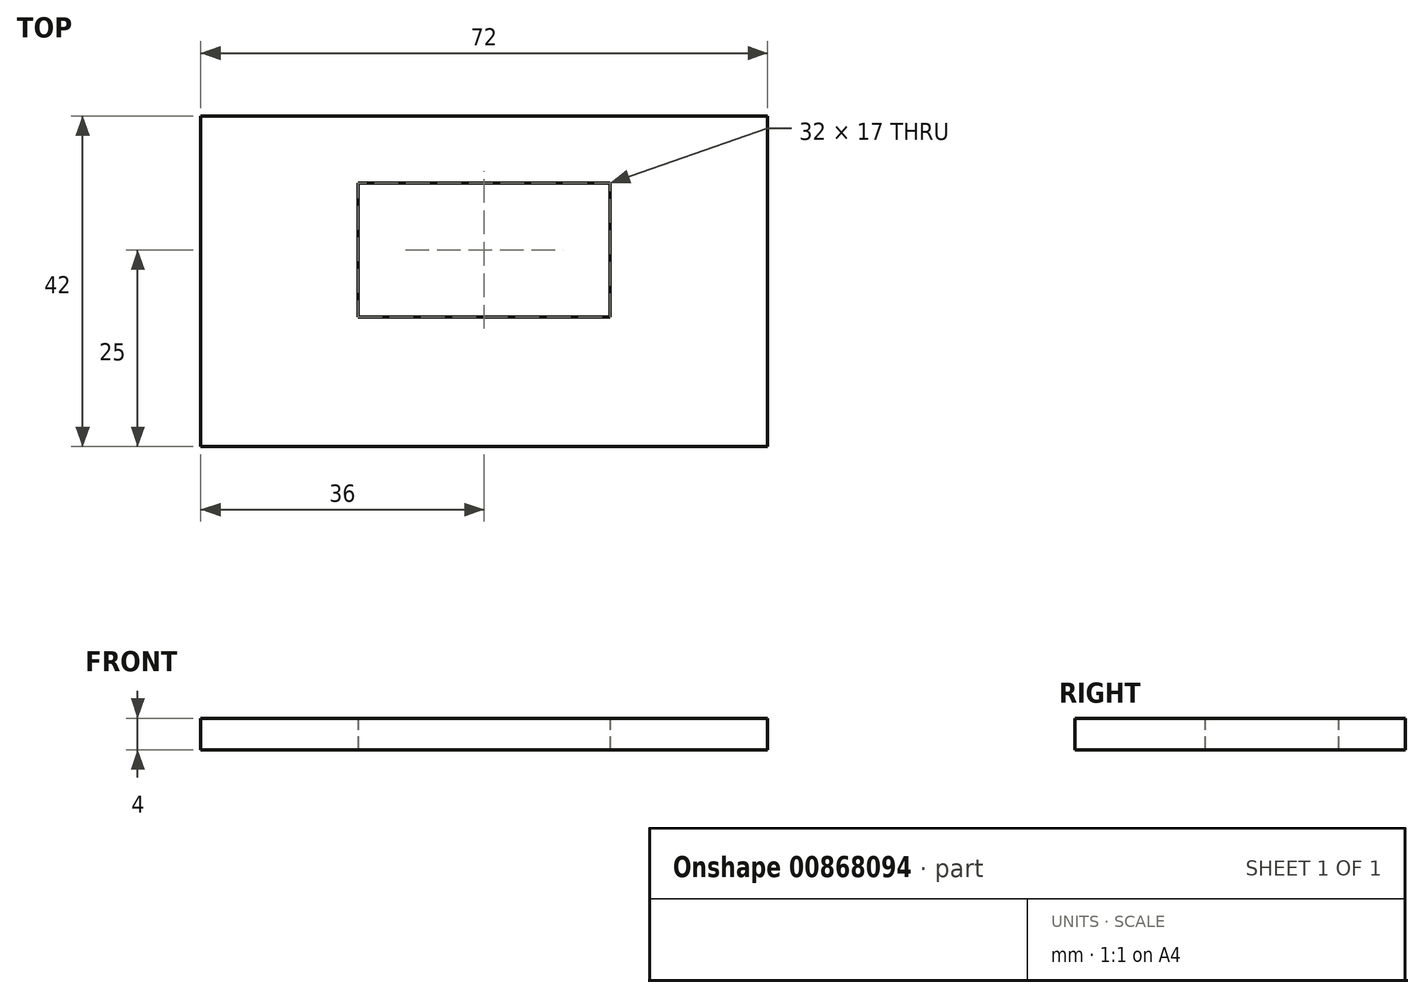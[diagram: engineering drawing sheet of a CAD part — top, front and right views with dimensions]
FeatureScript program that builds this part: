
annotation { "Feature Type Name" : "Feature", "Feature Type Description" : "" }
export const myFeature = defineFeature(function(context is Context, id is Id, definition is map)
    precondition{}
    {
        {
            var Q0;
            Q0=qCreatedBy(makeId("Top.planeOp"),FACE);
            var sketch = newSketch(context, id + "F0", { "sketchPlane" : qUnion([Q0])});
            skLineSegment(sketch, "E0.bottom", {"start": v(36, -21) * mm, "end": v(-36, -21) * mm});
            skLineSegment(sketch, "E0.top", {"start": v(36, 21) * mm, "end": v(-36, 21) * mm});
            skLineSegment(sketch, "E0.left", {"start": v(36, -21) * mm, "end": v(36, 21) * mm});
            skLineSegment(sketch, "E0.right", {"start": v(-36, -21) * mm, "end": v(-36, 21) * mm});
            skPoint(sketch, "E0.middle", {"position": v(0, 0) * mm});
            skLineSegment(sketch, "E1.bottom", {"start": v(-16, 12.5) * mm, "end": v(16, 12.5) * mm});
            skLineSegment(sketch, "E1.top", {"start": v(-16, -4.5) * mm, "end": v(16, -4.5) * mm});
            skLineSegment(sketch, "E1.left", {"start": v(-16, 12.5) * mm, "end": v(-16, -4.5) * mm});
            skLineSegment(sketch, "E1.right", {"start": v(16, 12.5) * mm, "end": v(16, -4.5) * mm});
            skSolve(sketch);
        }
        {
            var Q0;
            Q0 = qSketchRegion(id + "F0", true);
            extrude(context, id + "F1", {"entities" : qUnion([Q0]), "depth" : 4 * mm, "offsetDistance" : 25 * mm});
        }
    });
